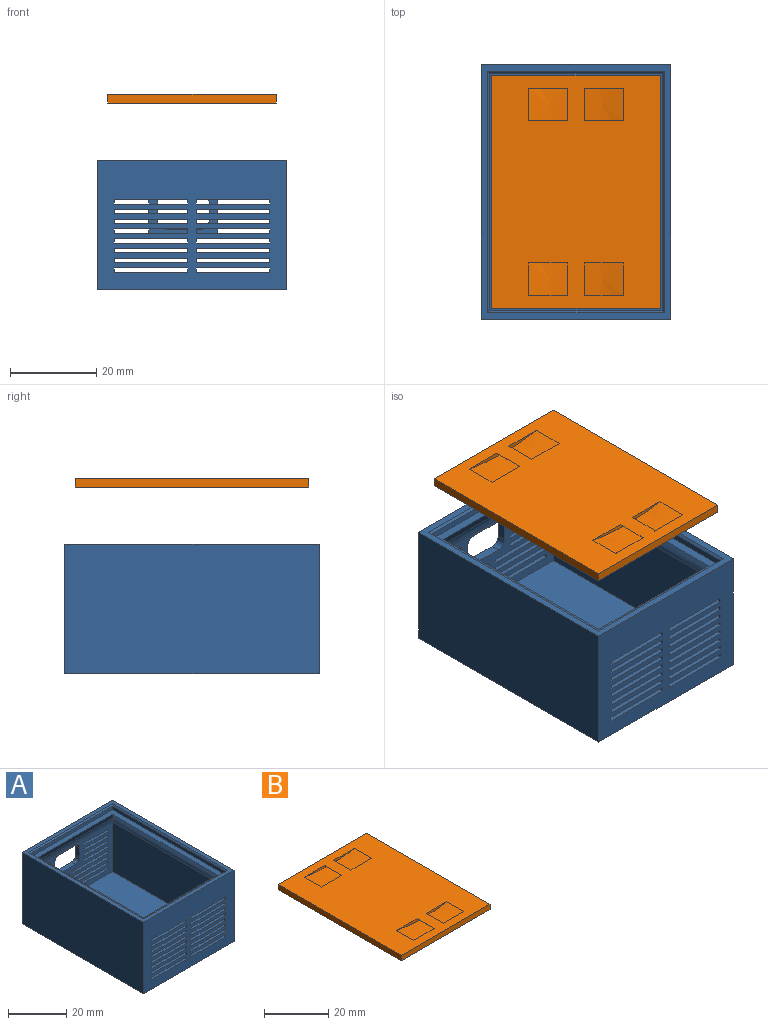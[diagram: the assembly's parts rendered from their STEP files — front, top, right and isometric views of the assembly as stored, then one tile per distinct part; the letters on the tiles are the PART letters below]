
ASSEMBLY  parts=2 mates=1
PART A: 179 faces, bbox 44.2x60.7x30.2 mm
  f0: plane 8x2mm, normal (0,0,-1), area 16mm2, adj f15,f25,f107,f171
  f1: plane 8x2mm, normal (0,0,1), area 16mm2, adj f15,f25,f107,f171
  f2: plane 8x2mm, normal (0,0,-1), area 16mm2, adj f15,f25,f128,f169
  f3: plane 8x2mm, normal (0,0,1), area 16mm2, adj f15,f25,f128,f169
  f4: plane 8.01x2mm, normal (0,0,-1), area 16mm2, adj f15,f25,f129,f168
  f5: plane 8.01x2mm, normal (0,0,1), area 16mm2, adj f15,f25,f129,f168
  f6: plane 8.01x2mm, normal (0,0,-1), area 16mm2, adj f15,f25,f130,f167
  f7: plane 8.01x2mm, normal (0,0,1), area 16mm2, adj f15,f25,f130,f167
  f8: plane 12x2mm, normal (0,0,-1), area 24mm2, adj f15,f25,f125,f170
  f9: plane 12x2mm, normal (0,0,-1), area 24mm2, adj f15,f25,f126,f174
  f10: plane 12x2mm, normal (0,0,1), area 24mm2, adj f15,f25,f126,f174
  f11: plane 12.01x2mm, normal (0,0,-1), area 24mm2, adj f15,f25,f127,f173
  f12: plane 12.01x2mm, normal (0,0,1), area 24mm2, adj f15,f25,f127,f173
  f13: plane 12.01x2mm, normal (0,0,-1), area 24mm2, adj f15,f25,f135,f172
  f14: plane 12.01x2mm, normal (0,0,1), area 24mm2, adj f15,f25,f135,f172
  f15: plane 40.21x21.03mm, normal (0,-1,0), area 523.4mm2, adj f0,f1,f2,f3,f4,f5,f6,f7
  f16: plane 59x44mm, normal (0,0,-1), area 916mm2, adj f24,f25,f26,f27,f148,f149,f150,f151
  f17: plane 55x1.5mm, normal (-1,0,0), area 82.5mm2, adj f28,f29,f32,f41
  f18: plane 38.94x2.94mm, normal (0,-0.89,-0.45), area 123.4mm2, adj f32,f33,f34,f37
  f19: plane 38.94x2.94mm, normal (0,0.89,-0.45), area 123.4mm2, adj f32,f33,f34,f36
  f20: plane 55x1.5mm, normal (1,0,0), area 82.5mm2, adj f28,f29,f32,f40
  f21: plane 55x20.82mm, normal (-1,0,0), area 1145.1mm2, adj f15,f22,f31,f38
  f22: plane 40x20.82mm, normal (0,1,0), area 560.8mm2, adj f21,f23,f31,f36,f43,f44,f45,f46
  f23: plane 55x20.82mm, normal (1,0,0), area 1145.1mm2, adj f15,f22,f31,f35
  f24: plane 59x30mm, normal (1,0,0), area 1770mm2, adj f16,f25,f27,f30
  f25: plane 44.21x30.21mm, normal (0,1,0), area 1010.6mm2, adj f0,f1,f2,f3,f4,f5,f6,f7
  f26: plane 59x30mm, normal (-1,0,0), area 1770mm2, adj f16,f25,f27,f30
  f27: plane 44x30mm, normal (0,-1,0), area 1048mm2, adj f16,f24,f26,f30,f43,f44,f45,f46
  f28: plane 40x1.5mm, normal (0,-1,0), area 60mm2, adj f17,f20,f32,f39
  f29: plane 40x1.5mm, normal (0,1,0), area 60mm2, adj f17,f20,f32,f42
  f30: plane 59x44mm, normal (0,0,1), area 300mm2, adj f24,f25,f26,f27,f39,f40,f41,f42
  f31: plane 55x40mm, normal (0,0,1), area 2200mm2, adj f15,f21,f22,f23
  f32: plane 55x40mm, normal (0,0,1), area 364mm2, adj f17,f18,f19,f20,f28,f29,f33,f34
  f33: plane 53.94x2.94mm, normal (0.89,0,-0.45), area 172.7mm2, adj f18,f19,f32,f35
  f34: plane 53.94x2.94mm, normal (-0.89,0,-0.45), area 172.7mm2, adj f18,f19,f32,f38
  f35: bspline ~60.5x2.24mm, area 126.3mm2, adj f23,f33,f36,f37
  f36: bspline ~44x2.24mm, area 91.5mm2, adj f19,f22,f35,f38
  f37: bspline ~44x2.24mm, area 91.5mm2, adj f15,f18,f35,f38
  f38: bspline ~60.5x2.24mm, area 126.3mm2, adj f21,f34,f36,f37
  f39: plane 41x0.5mm, normal (0,-0.71,0.71), area 28.6mm2, adj f28,f30,f40,f41
  f40: plane 56x0.5mm, normal (0.71,0,0.71), area 39.2mm2, adj f20,f30,f39,f42
  f41: plane 56x0.5mm, normal (-0.71,0,0.71), area 39.2mm2, adj f17,f30,f39,f42
  f42: plane 41x0.5mm, normal (0,0.71,0.71), area 28.6mm2, adj f29,f30,f40,f41
  f43: plane 2x1mm, normal (-1,0,0), area 2mm2, adj f22,f27,f44,f46
  f44: plane 17x2mm, normal (0,0,1), area 34mm2, adj f22,f27,f43,f45
  f45: plane 2x1mm, normal (1,0,0), area 2mm2, adj f22,f27,f44,f46
  f46: plane 17x2mm, normal (0,0,-1), area 34mm2, adj f22,f27,f43,f45
  f47: plane 2x1mm, normal (-1,0,0), area 2mm2, adj f22,f27,f48,f50
  f48: plane 17x2mm, normal (0,0,1), area 34mm2, adj f22,f27,f47,f49
  f49: plane 2x1mm, normal (1,0,0), area 2mm2, adj f22,f27,f48,f50
  f50: plane 17x2mm, normal (0,0,-1), area 34mm2, adj f22,f27,f47,f49
  f51: plane 2x1mm, normal (-1,0,0), area 2mm2, adj f22,f27,f52,f54
  f52: plane 17x2mm, normal (0,0,1), area 34mm2, adj f22,f27,f51,f53
  f53: plane 2x1mm, normal (1,0,0), area 2mm2, adj f22,f27,f52,f54
  f54: plane 17x2mm, normal (0,0,-1), area 34mm2, adj f22,f27,f51,f53
  f55: plane 2x1mm, normal (-1,0,0), area 2mm2, adj f22,f27,f56,f58
  f56: plane 17x2mm, normal (0,0,1), area 34mm2, adj f22,f27,f55,f57
  f57: plane 2x1mm, normal (1,0,0), area 2mm2, adj f22,f27,f56,f58
  f58: plane 17x2mm, normal (0,0,-1), area 34mm2, adj f22,f27,f55,f57
  f59: plane 2x1mm, normal (-1,0,0), area 2mm2, adj f22,f27,f60,f62
  f60: plane 17x2mm, normal (0,0,1), area 34mm2, adj f22,f27,f59,f61
  f61: plane 2x1mm, normal (1,0,0), area 2mm2, adj f22,f27,f60,f62
  f62: plane 17x2mm, normal (0,0,-1), area 34mm2, adj f22,f27,f59,f61
  f63: plane 2x1mm, normal (-1,0,0), area 2mm2, adj f22,f27,f64,f66
  f64: plane 17x2mm, normal (0,0,1), area 34mm2, adj f22,f27,f63,f65
  f65: plane 2x1mm, normal (1,0,0), area 2mm2, adj f22,f27,f64,f66
  f66: plane 17x2mm, normal (0,0,-1), area 34mm2, adj f22,f27,f63,f65
  f67: plane 2x1mm, normal (-1,0,0), area 2mm2, adj f22,f27,f68,f70
  f68: plane 17x2mm, normal (0,0,1), area 34mm2, adj f22,f27,f67,f69
  f69: plane 2x1mm, normal (1,0,0), area 2mm2, adj f22,f27,f68,f70
  f70: plane 17x2mm, normal (0,0,-1), area 34mm2, adj f22,f27,f67,f69
  f71: plane 2x1mm, normal (-1,0,0), area 2mm2, adj f22,f27,f72,f74
  f72: plane 17x2mm, normal (0,0,1), area 34mm2, adj f22,f27,f71,f73
  f73: plane 2x1mm, normal (1,0,0), area 2mm2, adj f22,f27,f72,f74
  f74: plane 17x2mm, normal (0,0,-1), area 34mm2, adj f22,f27,f71,f73
  f75: plane 2x1mm, normal (-1,0,0), area 2mm2, adj f22,f27,f76,f78
  f76: plane 17x2mm, normal (0,0,1), area 34mm2, adj f22,f27,f75,f77
  f77: plane 2x1mm, normal (1,0,0), area 2mm2, adj f22,f27,f76,f78
  f78: plane 17x2mm, normal (0,0,-1), area 34mm2, adj f22,f27,f75,f77
  f79: plane 2x1mm, normal (-1,0,0), area 2mm2, adj f22,f27,f80,f82
  f80: plane 17x2mm, normal (0,0,1), area 34mm2, adj f22,f27,f79,f81
  f81: plane 2x1mm, normal (1,0,0), area 2mm2, adj f22,f27,f80,f82
  f82: plane 17x2mm, normal (0,0,-1), area 34mm2, adj f22,f27,f79,f81
  f83: plane 2x1mm, normal (-1,0,0), area 2mm2, adj f22,f27,f84,f86
  f84: plane 17x2mm, normal (0,0,1), area 34mm2, adj f22,f27,f83,f85
  f85: plane 2x1mm, normal (1,0,0), area 2mm2, adj f22,f27,f84,f86
  f86: plane 17x2mm, normal (0,0,-1), area 34mm2, adj f22,f27,f83,f85
  f87: plane 2x1mm, normal (-1,0,0), area 2mm2, adj f22,f27,f88,f90
  f88: plane 17x2mm, normal (0,0,1), area 34mm2, adj f22,f27,f87,f89
  f89: plane 2x1mm, normal (1,0,0), area 2mm2, adj f22,f27,f88,f90
  f90: plane 17x2mm, normal (0,0,-1), area 34mm2, adj f22,f27,f87,f89
  f91: plane 2x1mm, normal (-1,0,0), area 2mm2, adj f22,f27,f92,f94
  f92: plane 17x2mm, normal (0,0,1), area 34mm2, adj f22,f27,f91,f93
  f93: plane 2x1mm, normal (1,0,0), area 2mm2, adj f22,f27,f92,f94
  f94: plane 17x2mm, normal (0,0,-1), area 34mm2, adj f22,f27,f91,f93
  f95: plane 2x1mm, normal (-1,0,0), area 2mm2, adj f22,f27,f96,f98
  f96: plane 17x2mm, normal (0,0,1), area 34mm2, adj f22,f27,f95,f97
  f97: plane 2x1mm, normal (1,0,0), area 2mm2, adj f22,f27,f96,f98
  f98: plane 17x2mm, normal (0,0,-1), area 34mm2, adj f22,f27,f95,f97
  f99: plane 2x1mm, normal (-1,0,0), area 2mm2, adj f22,f27,f100,f102
  f100: plane 17x2mm, normal (0,0,1), area 34mm2, adj f22,f27,f99,f101
  f101: plane 2x1mm, normal (1,0,0), area 2mm2, adj f22,f27,f100,f102
  f102: plane 17x2mm, normal (0,0,-1), area 34mm2, adj f22,f27,f99,f101
  f103: plane 2x1mm, normal (-1,0,0), area 2mm2, adj f22,f27,f104,f106
  f104: plane 17x2mm, normal (0,0,1), area 34mm2, adj f22,f27,f103,f105
  f105: plane 2x1mm, normal (1,0,0), area 2mm2, adj f22,f27,f104,f106
  f106: plane 17x2mm, normal (0,0,-1), area 34mm2, adj f22,f27,f103,f105
  f107: plane 2x1mm, normal (1,0,0), area 2mm2, adj f0,f1,f15,f25
  f108: plane 17x2mm, normal (0,0,-1), area 34mm2, adj f15,f25,f109,f111
  f109: plane 2x1mm, normal (1,0,0), area 2mm2, adj f15,f25,f108,f110
  f110: plane 17x2mm, normal (0,0,1), area 34mm2, adj f15,f25,f109,f111
  f111: plane 2x1mm, normal (-1,0,0), area 2mm2, adj f15,f25,f108,f110
  f112: plane 17x2mm, normal (0,0,-1), area 34mm2, adj f15,f25,f113,f115
  f113: plane 2x1mm, normal (1,0,0), area 2mm2, adj f15,f25,f112,f114
  f114: plane 17x2mm, normal (0,0,1), area 34mm2, adj f15,f25,f113,f115
  f115: plane 2x1mm, normal (-1,0,0), area 2mm2, adj f15,f25,f112,f114
  f116: plane 17x2mm, normal (0,0,-1), area 34mm2, adj f15,f25,f117,f119
  f117: plane 2x1mm, normal (1,0,0), area 2mm2, adj f15,f25,f116,f118
  f118: plane 17x2mm, normal (0,0,1), area 34mm2, adj f15,f25,f117,f119
  f119: plane 2x1mm, normal (-1,0,0), area 2mm2, adj f15,f25,f116,f118
  f120: plane 17x2mm, normal (0,0,-1), area 34mm2, adj f15,f25,f121,f123
  f121: plane 2x1mm, normal (1,0,0), area 2mm2, adj f15,f25,f120,f122
  f122: plane 17x2mm, normal (0,0,1), area 34mm2, adj f15,f25,f121,f123
  f123: plane 2x1mm, normal (-1,0,0), area 2mm2, adj f15,f25,f120,f122
  f124: plane 12x2mm, normal (0,0,1), area 24mm2, adj f15,f25,f125,f170
  f125: plane 2x1mm, normal (-1,0,0), area 2mm2, adj f8,f15,f25,f124
  f126: plane 2x1mm, normal (-1,0,0), area 2mm2, adj f9,f10,f15,f25
  f127: plane 2x1mm, normal (-1,0,0), area 2mm2, adj f11,f12,f15,f25
  f128: plane 2x1mm, normal (1,0,0), area 2mm2, adj f2,f3,f15,f25
  f129: plane 2x1mm, normal (1,0,0), area 2mm2, adj f4,f5,f15,f25
  f130: plane 2x1mm, normal (1,0,0), area 2mm2, adj f6,f7,f15,f25
  f131: plane 17x2mm, normal (0,0,-1), area 34mm2, adj f15,f25,f132,f134
  f132: plane 2x1mm, normal (1,0,0), area 2mm2, adj f15,f25,f131,f133
  f133: plane 17x2mm, normal (0,0,1), area 34mm2, adj f15,f25,f132,f134
  f134: plane 2x1mm, normal (-1,0,0), area 2mm2, adj f15,f25,f131,f133
  f135: plane 2x1mm, normal (-1,0,0), area 2mm2, adj f13,f14,f15,f25
  f136: plane 17x2mm, normal (0,0,-1), area 34mm2, adj f15,f25,f137,f139
  f137: plane 2x1mm, normal (1,0,0), area 2mm2, adj f15,f25,f136,f138
  f138: plane 17x2mm, normal (0,0,1), area 34mm2, adj f15,f25,f137,f139
  f139: plane 2x1mm, normal (-1,0,0), area 2mm2, adj f15,f25,f136,f138
  f140: plane 17x2mm, normal (0,0,-1), area 34mm2, adj f15,f25,f141,f143
  f141: plane 2x1mm, normal (1,0,0), area 2mm2, adj f15,f25,f140,f142
  f142: plane 17x2mm, normal (0,0,1), area 34mm2, adj f15,f25,f141,f143
  f143: plane 2x1mm, normal (-1,0,0), area 2mm2, adj f15,f25,f140,f142
  f144: plane 17x2mm, normal (0,0,-1), area 34mm2, adj f15,f25,f145,f147
  f145: plane 2x1mm, normal (1,0,0), area 2mm2, adj f15,f25,f144,f146
  f146: plane 17x2mm, normal (0,0,1), area 34mm2, adj f15,f25,f145,f147
  f147: plane 2x1mm, normal (-1,0,0), area 2mm2, adj f15,f25,f144,f146
  f148: plane 14x1mm, normal (1,0,0), area 14mm2, adj f16,f149,f151,f152
  f149: plane 40x1mm, normal (0,1,0), area 40mm2, adj f16,f148,f150,f152
  f150: plane 14x1mm, normal (-1,0,0), area 14mm2, adj f16,f149,f151,f152
  f151: plane 40x1mm, normal (0,-1,0), area 40mm2, adj f16,f148,f150,f152
  f152: plane 40x14mm, normal (0,0,-1), area 560mm2, adj f148,f149,f150,f151
  f153: plane 14x1mm, normal (1,0,0), area 14mm2, adj f16,f154,f156,f157
  f154: plane 40x1mm, normal (0,1,0), area 40mm2, adj f16,f153,f155,f157
  f155: plane 14x1mm, normal (-1,0,0), area 14mm2, adj f16,f154,f156,f157
  f156: plane 40x1mm, normal (0,-1,0), area 40mm2, adj f16,f153,f155,f157
  f157: plane 40x14mm, normal (0,0,-1), area 560mm2, adj f153,f154,f155,f156
  f158: plane 40x1mm, normal (0,-1,0), area 40mm2, adj f16,f159,f161,f162
  f159: plane 14x1mm, normal (1,0,0), area 14mm2, adj f16,f158,f160,f162
  f160: plane 40x1mm, normal (0,1,0), area 40mm2, adj f16,f159,f161,f162
  f161: plane 14x1mm, normal (-1,0,0), area 14mm2, adj f16,f158,f160,f162
  f162: plane 40x14mm, normal (0,0,-1), area 560mm2, adj f158,f159,f160,f161
  f163: plane 4x2mm, normal (1,0,0), area 8mm2, adj f15,f25,f176,f178
  f164: plane 8x2mm, normal (0,0,-1), area 16mm2, adj f15,f25,f177,f178
  f165: plane 4x2mm, normal (-1,0,0), area 8mm2, adj f15,f25,f175,f177
  f166: plane 8x2mm, normal (0,0,1), area 16mm2, adj f15,f25,f175,f176
  f167: plane 2x1mm, normal (-1,0,0), area 2mm2, adj f6,f7,f15,f25
  f168: plane 2x1mm, normal (-1,0,0), area 2mm2, adj f4,f5,f15,f25
  f169: plane 2x1mm, normal (-1,0,0), area 2mm2, adj f2,f3,f15,f25
  f170: plane 2x1mm, normal (1,0,0), area 2mm2, adj f8,f15,f25,f124
  f171: plane 2x1mm, normal (-1,0,0), area 2mm2, adj f0,f1,f15,f25
  f172: plane 2x1mm, normal (1,0,0), area 2mm2, adj f13,f14,f15,f25
  f173: plane 2x1mm, normal (1,0,0), area 2mm2, adj f11,f12,f15,f25
  f174: plane 2x1mm, normal (1,0,0), area 2mm2, adj f9,f10,f15,f25
  f175: bspline ~2.2x2mm, area 6.5mm2, adj f15,f25,f165,f166
  f176: bspline ~2.2x2mm, area 6.5mm2, adj f15,f25,f163,f166
  f177: bspline ~2.2x2mm, area 6.5mm2, adj f15,f25,f164,f165
  f178: bspline ~2.2x2mm, area 6.5mm2, adj f15,f25,f163,f164
PART B: 25 faces, bbox 39x54x2 mm
  f0: plane 54x39mm, normal (0,0,1), area 1836mm2, adj f1,f2,f3,f4,f9,f10,f11,f12
  f1: plane 39x2mm, normal (0,1,0), area 78mm2, adj f0,f2,f4,f5
  f2: plane 54x2mm, normal (-1,0,0), area 108mm2, adj f0,f1,f3,f5
  f3: plane 39x2mm, normal (0,-1,0), area 78mm2, adj f0,f2,f4,f5
  f4: plane 54x2mm, normal (1,0,0), area 108mm2, adj f0,f1,f3,f5
  f5: plane 54x39mm, normal (0,0,-1), area 1490.2mm2, adj f1,f2,f3,f4,f8
  f6: plane 28x28mm, normal (0,0,-1), area 587.5mm2, adj f7,f8
  f7: revolved ~6x6mm, area 29.2mm2, adj f6
  f8: cylinder r=14mm len=28mm, axis (0,0,-1), area 88mm2, adj f5,f6
  f9: plane 7.5x1mm, normal (-0.71,0,-0.71), area 10.6mm2, adj f0,f10,f11,f12
  f10: extruded ~10x7.5mm, area 75.5mm2, adj f0,f9,f11,f12
  f11: plane 10x1mm, normal (0,-1,0), area 6.2mm2, adj f0,f9,f10
  f12: plane 10x1mm, normal (0,1,0), area 6.2mm2, adj f0,f9,f10
  f13: plane 7.5x1mm, normal (0.71,0,-0.71), area 10.6mm2, adj f0,f14,f15,f16
  f14: extruded ~10x7.5mm, area 75.5mm2, adj f0,f13,f15,f16
  f15: plane 10x1mm, normal (0,-1,0), area 6.2mm2, adj f0,f13,f14
  f16: plane 10x1mm, normal (0,1,0), area 6.2mm2, adj f0,f13,f14
  f17: plane 7.5x1mm, normal (-0.71,0,-0.71), area 10.6mm2, adj f0,f18,f19,f20
  f18: extruded ~10x7.5mm, area 75.5mm2, adj f0,f17,f19,f20
  f19: plane 10x1mm, normal (0,1,0), area 6.2mm2, adj f0,f17,f18
  f20: plane 10x1mm, normal (0,-1,0), area 6.2mm2, adj f0,f17,f18
  f21: extruded ~10x7.5mm, area 75.5mm2, adj f0,f22,f23,f24
  f22: plane 7.5x1mm, normal (0.71,0,-0.71), area 10.6mm2, adj f0,f21,f23,f24
  f23: plane 10x1mm, normal (0,1,0), area 6.2mm2, adj f0,f21,f22
  f24: plane 10x1mm, normal (0,-1,0), area 6.2mm2, adj f0,f21,f22
PLACE A t=(45.43,-61.38,1.1)mm fixed
PLACE B t=(23.43,-31.88,44.32)mm
MATE slider A.f32 <-> B.f8  axis (0,0,1) through (23.43,-31.88,29.1)mm
